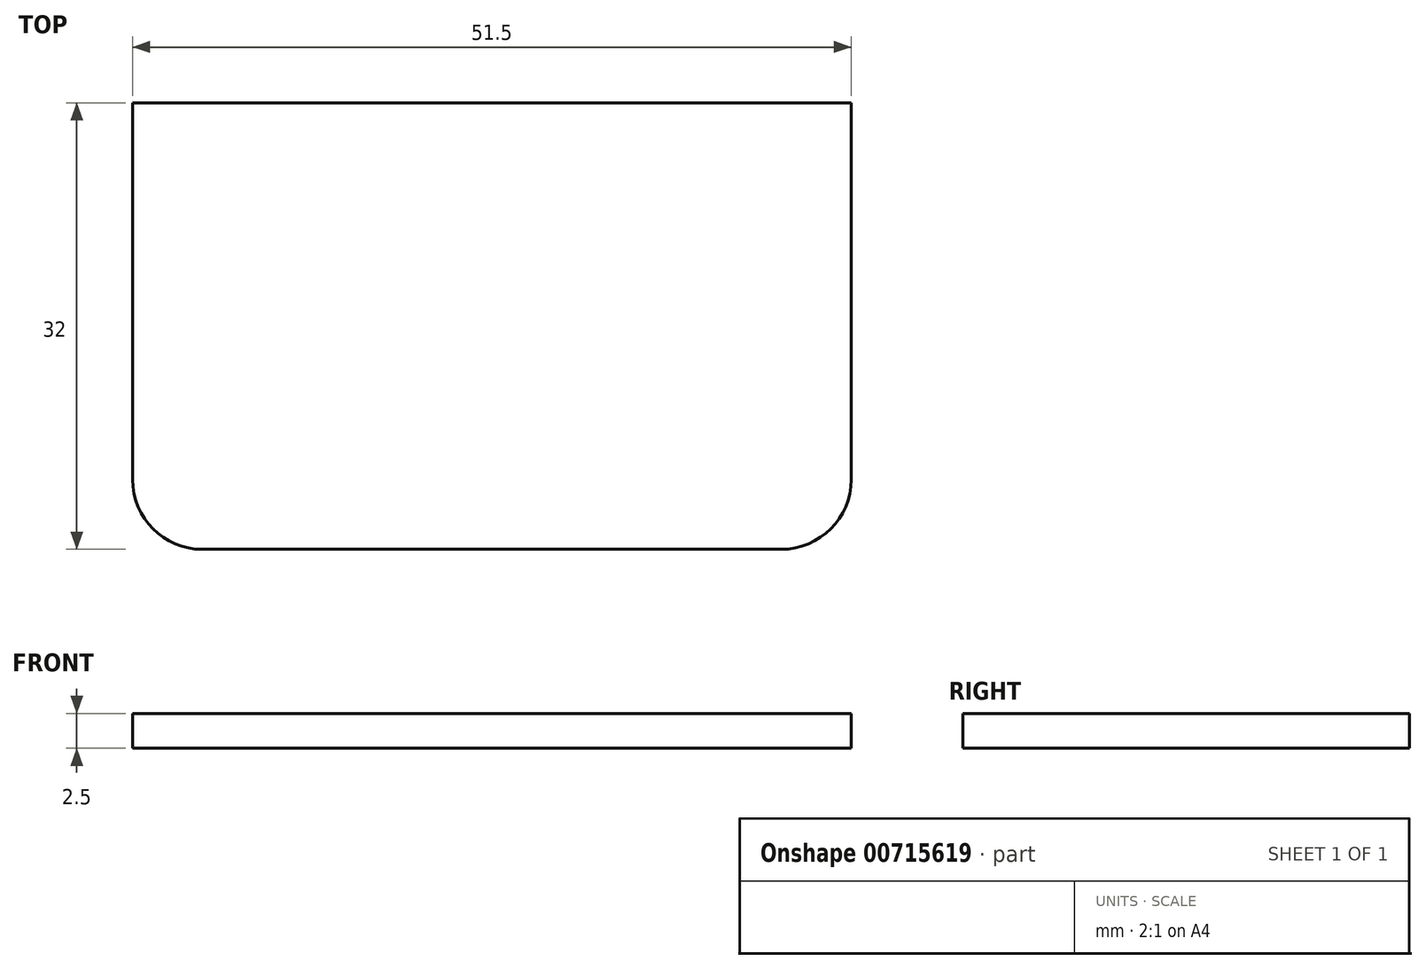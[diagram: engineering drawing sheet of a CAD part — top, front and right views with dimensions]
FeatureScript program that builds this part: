
annotation { "Feature Type Name" : "Feature", "Feature Type Description" : "" }
export const myFeature = defineFeature(function(context is Context, id is Id, definition is map)
    precondition{}
    {
        {
            var Q0;
            Q0=qCreatedBy(makeId("Top.planeOp"),FACE);
            var sketch = newSketch(context, id + "F0", { "sketchPlane" : qUnion([Q0])});
            skLineSegment(sketch, "E0.bottom", {"start": v(-20.75, -16) * mm, "end": v(20.75, -16) * mm});
            skLineSegment(sketch, "E0.top", {"start": v(-25.75, 16) * mm, "end": v(25.75, 16) * mm});
            skLineSegment(sketch, "E0.left", {"start": v(-25.75, -11) * mm, "end": v(-25.75, 16) * mm});
            skLineSegment(sketch, "E0.right", {"start": v(25.75, -11) * mm, "end": v(25.75, 16) * mm});
            skPoint(sketch, "E0.middle", {"position": v(0, 0) * mm});
            skPoint(sketch, "E1.visualSharp", {"position": v(-25.75, -16) * mm});
            skArc(sketch, "E1.filletArc", {"start": v(-25.75, -11) * mm, "mid": v(-24.29, -14.54) * mm, "end": v(-20.75, -16) * mm});
            skPoint(sketch, "E2.visualSharp", {"position": v(25.75, -16) * mm});
            skArc(sketch, "E2.filletArc", {"start": v(20.75, -16) * mm, "mid": v(24.29, -14.54) * mm, "end": v(25.75, -11) * mm});
            skLineSegment(sketch, "E3", {"start": v(-25.75, -16) * mm, "end": v(-25.75, 11.5) * mm, "construction": true});
            skSolve(sketch);
        }
        {
            var Q0;
            Q0=makeQuery(id+"F0.imprint","IMPRINT",FACE,{"disambiguationData":[TD([[makeQuery(id+"F0.imprint","IMPRINT",EDGE,{"derivedFrom":sQuery(id+"F0.wireOp",EDGE,"E0.bottom")}),1.0]])]});
            extrude(context, id + "F1", {"entities" : qUnion([Q0]), "depth" : 2.5 * mm, "offsetDistance" : 25 * mm});
        }
    });
